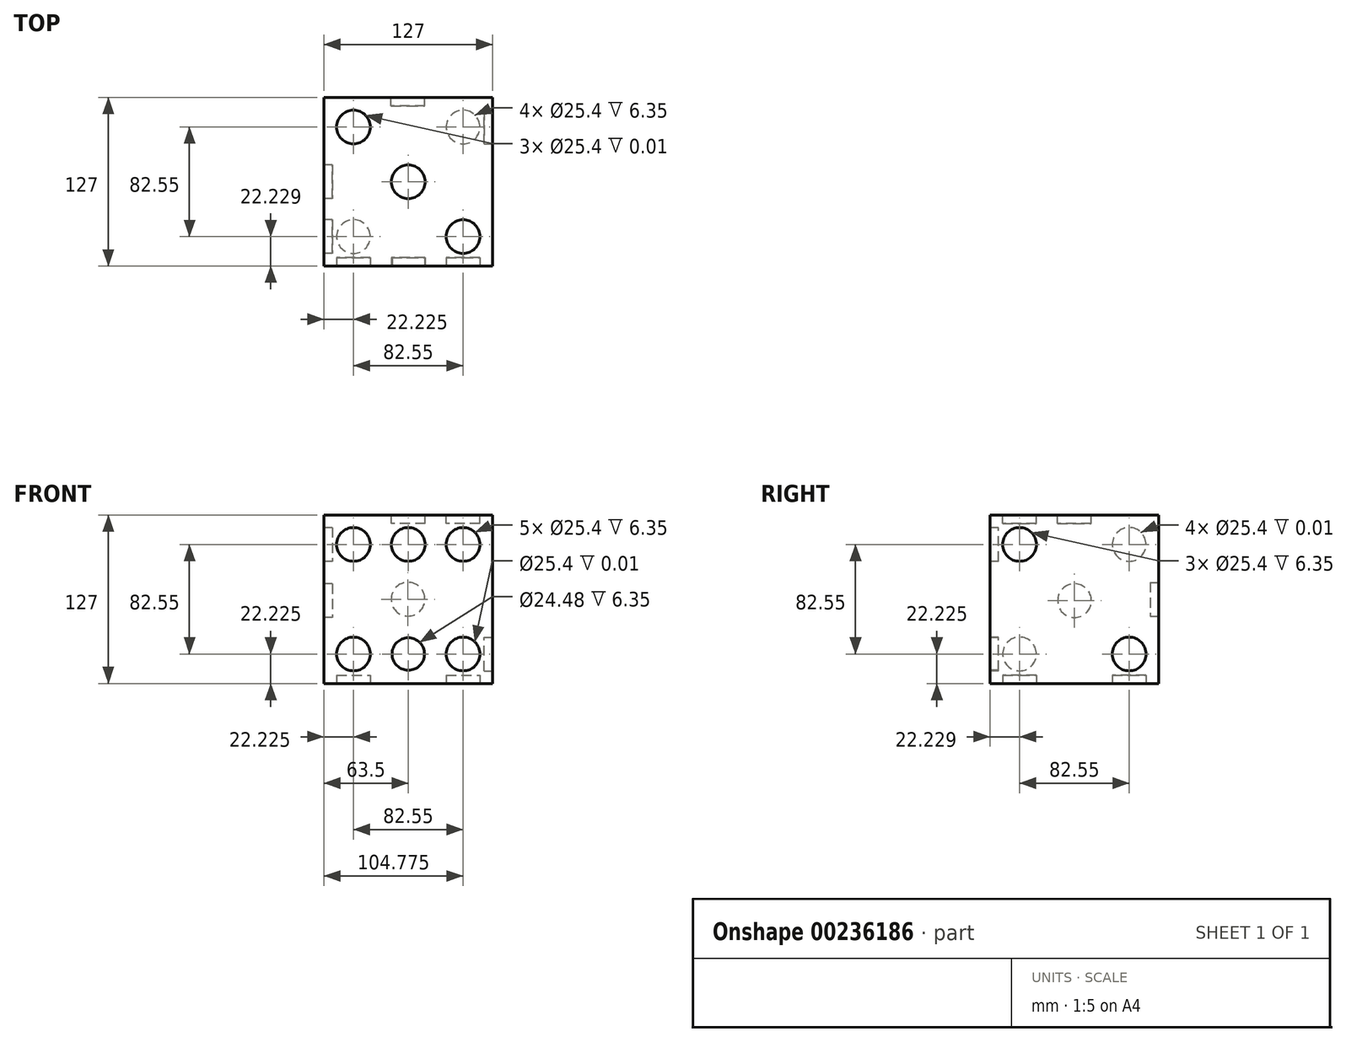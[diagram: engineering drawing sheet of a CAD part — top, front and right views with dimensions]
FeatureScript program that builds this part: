
annotation { "Feature Type Name" : "Feature", "Feature Type Description" : "" }
export const myFeature = defineFeature(function(context is Context, id is Id, definition is map)
    precondition{}
    {
        {
            var Q0;
            Q0=qCreatedBy(makeId("Right.planeOp"),FACE);
            var sketch = newSketch(context, id + "F0", { "sketchPlane" : qUnion([Q0])});
            skLineSegment(sketch, "E0.bottom", {"start": v(-65.66, 58.24) * mm, "end": v(61.34, 58.24) * mm});
            skLineSegment(sketch, "E0.top", {"start": v(-65.66, -68.76) * mm, "end": v(61.34, -68.76) * mm});
            skLineSegment(sketch, "E0.left", {"start": v(-65.66, 58.24) * mm, "end": v(-65.66, -68.76) * mm});
            skLineSegment(sketch, "E0.right", {"start": v(61.34, 58.24) * mm, "end": v(61.34, -68.76) * mm});
            skSolve(sketch);
        }
        {
            var Q0;
            Q0 = qSketchRegion(id + "F0", true);
            var Q1;
            Q1=makeQuery(id+"F0.imprint","IMPRINT",FACE,{"disambiguationData":[TD([[makeQuery(id+"F0.imprint","IMPRINT",EDGE,{"derivedFrom":sQuery(id+"F0.wireOp",EDGE,"E0.bottom")}),-1.0]])]});
            extrude(context, id + "F1", {"entities" : qUnion([Q0, Q1]), "depth" : 127 * mm});
        }
        {
            var Q0;
            Q0=makeQuery(id+"F1.opExtrude","SWEPT_FACE",FACE,{"disambiguationData":[OSD([sQuery(id+"F0.wireOp",EDGE,"E0.right")])]});
            var sketch = newSketch(context, id + "F2", { "sketchPlane" : qUnion([Q0])});
            skCircle(sketch, "E1", {"center": v(-63.28, -5.26) * mm, "radius": 12.7 * mm});
            skSolve(sketch);
        }
        {
            var Q0;
            Q0 = qSketchRegion(id + "F2", true);
            extrude(context, id + "F3", {"entities" : qUnion([Q0]), "operationType" : NewBodyOperationType.REMOVE, "oppositeDirection" : true, "depth" : 6.35 * mm});
        }
        {
            var Q0;
            Q0=makeQuery(id+"F1.opExtrude","CAP_FACE",FACE,{"disambiguationData":[OSD([sQuery(id+"F0.wireOp",EDGE,"E0.bottom"),sQuery(id+"F0.wireOp",EDGE,"E0.top"),sQuery(id+"F0.wireOp",EDGE,"E0.left"),sQuery(id+"F0.wireOp",EDGE,"E0.right")])],"isStart":true});
            var sketch = newSketch(context, id + "F4", { "sketchPlane" : qUnion([Q0])});
            skCircle(sketch, "E2", {"center": v(2.03, -6.35) * mm, "radius": 12.7 * mm});
            skSolve(sketch);
        }
        {
            var Q0;
            Q0 = qSketchRegion(id + "F4", true);
            extrude(context, id + "F5", {"entities" : qUnion([Q0]), "operationType" : NewBodyOperationType.REMOVE, "oppositeDirection" : true, "depth" : 6.35 * mm});
        }
        {
            var Q0;
            Q0=makeQuery(id+"F1.opExtrude","CAP_FACE",FACE,{"disambiguationData":[OSD([sQuery(id+"F0.wireOp",EDGE,"E0.bottom"),sQuery(id+"F0.wireOp",EDGE,"E0.top"),sQuery(id+"F0.wireOp",EDGE,"E0.left"),sQuery(id+"F0.wireOp",EDGE,"E0.right")])],"isStart":true});
            var sketch = newSketch(context, id + "F6", { "sketchPlane" : qUnion([Q0])});
            skCircle(sketch, "E3", {"center": v(-39.12, 36.01) * mm, "radius": 12.7 * mm});
            skSolve(sketch);
        }
        {
            var Q0;
            Q0 = qSketchRegion(id + "F6", true);
            extrude(context, id + "F7", {"entities" : qUnion([Q0]), "operationType" : NewBodyOperationType.REMOVE, "oppositeDirection" : true, "depth" : 1 / 101.6 * mm});
        }
        {
            var Q0;
            Q0=makeQuery(id+"F1.opExtrude","CAP_FACE",FACE,{"disambiguationData":[OSD([sQuery(id+"F0.wireOp",EDGE,"E0.bottom"),sQuery(id+"F0.wireOp",EDGE,"E0.top"),sQuery(id+"F0.wireOp",EDGE,"E0.left"),sQuery(id+"F0.wireOp",EDGE,"E0.right")])],"isStart":true});
            var sketch = newSketch(context, id + "F8", { "sketchPlane" : qUnion([Q0])});
            skCircle(sketch, "E4", {"center": v(43.43, 36.01) * mm, "radius": 12.7 * mm});
            skSolve(sketch);
        }
        {
            var Q0;
            Q0 = qSketchRegion(id + "F8", true);
            extrude(context, id + "F9", {"entities" : qUnion([Q0]), "operationType" : NewBodyOperationType.REMOVE, "oppositeDirection" : true, "depth" : 6.35 * mm});
        }
        {
            var Q0;
            Q0=makeQuery(id+"F1.opExtrude","CAP_FACE",FACE,{"disambiguationData":[OSD([sQuery(id+"F0.wireOp",EDGE,"E0.bottom"),sQuery(id+"F0.wireOp",EDGE,"E0.top"),sQuery(id+"F0.wireOp",EDGE,"E0.left"),sQuery(id+"F0.wireOp",EDGE,"E0.right")])],"isStart":true});
            var sketch = newSketch(context, id + "F10", { "sketchPlane" : qUnion([Q0])});
            skCircle(sketch, "E5", {"center": v(-39.12, -46.54) * mm, "radius": 12.7 * mm});
            skSolve(sketch);
        }
        {
            var Q0;
            Q0 = qSketchRegion(id + "F10", true);
            extrude(context, id + "F11", {"entities" : qUnion([Q0]), "operationType" : NewBodyOperationType.REMOVE, "oppositeDirection" : true, "depth" : 1 / 101.6 * mm});
        }
        {
            var Q0;
            Q0=makeQuery(id+"F1.opExtrude","CAP_FACE",FACE,{"disambiguationData":[OSD([sQuery(id+"F0.wireOp",EDGE,"E0.bottom"),sQuery(id+"F0.wireOp",EDGE,"E0.top"),sQuery(id+"F0.wireOp",EDGE,"E0.left"),sQuery(id+"F0.wireOp",EDGE,"E0.right")])],"isStart":true});
            var sketch = newSketch(context, id + "F12", { "sketchPlane" : qUnion([Q0])});
            skCircle(sketch, "E6", {"center": v(43.43, -46.54) * mm, "radius": 12.7 * mm});
            skSolve(sketch);
        }
        {
            var Q0;
            Q0 = qSketchRegion(id + "F12", true);
            extrude(context, id + "F13", {"entities" : qUnion([Q0]), "operationType" : NewBodyOperationType.REMOVE, "oppositeDirection" : true, "depth" : 1 / 101.6 * mm});
        }
        {
            var Q0;
            Q0=makeQuery(id+"F1.opExtrude","CAP_FACE",FACE,{"disambiguationData":[OSD([sQuery(id+"F0.wireOp",EDGE,"E0.bottom"),sQuery(id+"F0.wireOp",EDGE,"E0.top"),sQuery(id+"F0.wireOp",EDGE,"E0.left"),sQuery(id+"F0.wireOp",EDGE,"E0.right")])],"isStart":false});
            var sketch = newSketch(context, id + "F14", { "sketchPlane" : qUnion([Q0])});
            skCircle(sketch, "E7", {"center": v(39.12, -46.54) * mm, "radius": 12.7 * mm});
            skSolve(sketch);
        }
        {
            var Q0;
            Q0 = qSketchRegion(id + "F14", true);
            extrude(context, id + "F15", {"entities" : qUnion([Q0]), "operationType" : NewBodyOperationType.REMOVE, "oppositeDirection" : true, "depth" : 6.35 * mm});
        }
        {
            var Q0;
            Q0=makeQuery(id+"F1.opExtrude","CAP_FACE",FACE,{"disambiguationData":[OSD([sQuery(id+"F0.wireOp",EDGE,"E0.bottom"),sQuery(id+"F0.wireOp",EDGE,"E0.top"),sQuery(id+"F0.wireOp",EDGE,"E0.left"),sQuery(id+"F0.wireOp",EDGE,"E0.right")])],"isStart":false});
            var sketch = newSketch(context, id + "F16", { "sketchPlane" : qUnion([Q0])});
            skCircle(sketch, "E8", {"center": v(-43.43, 36.01) * mm, "radius": 12.7 * mm});
            skSolve(sketch);
        }
        {
            var Q0;
            Q0 = qSketchRegion(id + "F16", true);
            extrude(context, id + "F17", {"entities" : qUnion([Q0]), "operationType" : NewBodyOperationType.REMOVE, "oppositeDirection" : true, "depth" : 1 / 101.6 * mm});
        }
        {
            var Q0;
            Q0=makeQuery(id+"F1.opExtrude","SWEPT_FACE",FACE,{"disambiguationData":[OSD([sQuery(id+"F0.wireOp",EDGE,"E0.left")])]});
            var sketch = newSketch(context, id + "F18", { "sketchPlane" : qUnion([Q0])});
            skCircle(sketch, "E9", {"center": v(104.78, -46.54) * mm, "radius": 12.7 * mm});
            skSolve(sketch);
        }
        {
            var Q0;
            Q0 = qSketchRegion(id + "F18", true);
            extrude(context, id + "F19", {"entities" : qUnion([Q0]), "operationType" : NewBodyOperationType.REMOVE, "oppositeDirection" : true, "depth" : 1 / 101.6 * mm});
        }
        {
            var Q0;
            Q0=makeQuery(id+"F1.opExtrude","SWEPT_FACE",FACE,{"disambiguationData":[OSD([sQuery(id+"F0.wireOp",EDGE,"E0.left")])]});
            var sketch = newSketch(context, id + "F20", { "sketchPlane" : qUnion([Q0])});
            skCircle(sketch, "E10", {"center": v(63.5, -46.54) * mm, "radius": 12.24 * mm});
            skSolve(sketch);
        }
        {
            var Q0;
            Q0 = qSketchRegion(id + "F20", true);
            extrude(context, id + "F21", {"entities" : qUnion([Q0]), "operationType" : NewBodyOperationType.REMOVE, "oppositeDirection" : true, "depth" : 6.35 * mm});
        }
        {
            var Q0;
            Q0=makeQuery(id+"F1.opExtrude","SWEPT_FACE",FACE,{"disambiguationData":[OSD([sQuery(id+"F0.wireOp",EDGE,"E0.left")])]});
            var sketch = newSketch(context, id + "F22", { "sketchPlane" : qUnion([Q0])});
            skCircle(sketch, "E11", {"center": v(22.23, -46.54) * mm, "radius": 12.7 * mm});
            skSolve(sketch);
        }
        {
            var Q0;
            Q0 = qSketchRegion(id + "F22", true);
            extrude(context, id + "F23", {"entities" : qUnion([Q0]), "operationType" : NewBodyOperationType.REMOVE, "oppositeDirection" : true, "depth" : 6.35 * mm});
        }
        {
            var Q0;
            Q0=makeQuery(id+"F1.opExtrude","SWEPT_FACE",FACE,{"disambiguationData":[OSD([sQuery(id+"F0.wireOp",EDGE,"E0.left")])]});
            var sketch = newSketch(context, id + "F24", { "sketchPlane" : qUnion([Q0])});
            skSolve(sketch);
        }
        {
            var Q0;
            {var subQ0=sQuery(id+"F0.wireOp",EDGE,"E0.left");Q0=makeQuery(id+"F24.imprint","IMPRINT",FACE,{"disambiguationData":[TD([[makeQuery(id+"F24.imprint","IMPRINT",EDGE,{"derivedFrom":makeQuery(id+"F1.opExtrude","CAP_EDGE",EDGE,{"disambiguationData":[OSD([subQ0])],"isStart":true})}),1.0]])]});}
            var sketch = newSketch(context, id + "F25", { "sketchPlane" : qUnion([Q0])});
            skCircle(sketch, "E12", {"center": v(104.78, 36.01) * mm, "radius": 12.7 * mm});
            skSolve(sketch);
        }
        {
            var Q0;
            Q0 = qSketchRegion(id + "F25", true);
            extrude(context, id + "F26", {"entities" : qUnion([Q0]), "operationType" : NewBodyOperationType.REMOVE, "oppositeDirection" : true, "depth" : 6.35 * mm});
        }
        {
            var Q0;
            {var subQ0=sQuery(id+"F0.wireOp",EDGE,"E0.left");Q0=makeQuery(id+"F24.imprint","IMPRINT",FACE,{"disambiguationData":[TD([[makeQuery(id+"F24.imprint","IMPRINT",EDGE,{"derivedFrom":makeQuery(id+"F1.opExtrude","CAP_EDGE",EDGE,{"disambiguationData":[OSD([subQ0])],"isStart":true})}),1.0]])]});}
            var sketch = newSketch(context, id + "F27", { "sketchPlane" : qUnion([Q0])});
            skCircle(sketch, "E13", {"center": v(63.5, 36.01) * mm, "radius": 12.7 * mm});
            skSolve(sketch);
        }
        {
            var Q0;
            Q0 = qSketchRegion(id + "F27", true);
            extrude(context, id + "F28", {"entities" : qUnion([Q0]), "operationType" : NewBodyOperationType.REMOVE, "oppositeDirection" : true, "depth" : 6.35 * mm});
        }
        {
            var Q0;
            {var subQ0=sQuery(id+"F0.wireOp",EDGE,"E0.left");Q0=makeQuery(id+"F24.imprint","IMPRINT",FACE,{"disambiguationData":[TD([[makeQuery(id+"F24.imprint","IMPRINT",EDGE,{"derivedFrom":makeQuery(id+"F1.opExtrude","CAP_EDGE",EDGE,{"disambiguationData":[OSD([subQ0])],"isStart":true})}),1.0]])]});}
            var sketch = newSketch(context, id + "F29", { "sketchPlane" : qUnion([Q0])});
            skCircle(sketch, "E14", {"center": v(22.23, 36.01) * mm, "radius": 12.7 * mm});
            skSolve(sketch);
        }
        {
            var Q0;
            Q0 = qSketchRegion(id + "F29", true);
            extrude(context, id + "F30", {"entities" : qUnion([Q0]), "operationType" : NewBodyOperationType.REMOVE, "oppositeDirection" : true, "depth" : 6.35 * mm});
        }
        {
            var Q0;
            Q0=makeQuery(id+"F1.opExtrude","SWEPT_FACE",FACE,{"disambiguationData":[OSD([sQuery(id+"F0.wireOp",EDGE,"E0.bottom")])]});
            var sketch = newSketch(context, id + "F31", { "sketchPlane" : qUnion([Q0])});
            skCircle(sketch, "E15", {"center": v(104.78, -43.43) * mm, "radius": 12.7 * mm});
            skSolve(sketch);
        }
        {
            var Q0;
            Q0 = qSketchRegion(id + "F31", true);
            extrude(context, id + "F32", {"entities" : qUnion([Q0]), "operationType" : NewBodyOperationType.REMOVE, "oppositeDirection" : true, "depth" : 6.35 * mm});
        }
        {
            var Q0;
            Q0=makeQuery(id+"F1.opExtrude","SWEPT_FACE",FACE,{"disambiguationData":[OSD([sQuery(id+"F0.wireOp",EDGE,"E0.bottom")])]});
            var sketch = newSketch(context, id + "F33", { "sketchPlane" : qUnion([Q0])});
            skCircle(sketch, "E16", {"center": v(63.5, -2.16) * mm, "radius": 12.7 * mm});
            skSolve(sketch);
        }
        {
            var Q0;
            Q0 = qSketchRegion(id + "F33", true);
            extrude(context, id + "F34", {"entities" : qUnion([Q0]), "operationType" : NewBodyOperationType.REMOVE, "oppositeDirection" : true, "depth" : 6.35 * mm});
        }
        {
            var Q0;
            Q0=makeQuery(id+"F1.opExtrude","SWEPT_FACE",FACE,{"disambiguationData":[OSD([sQuery(id+"F0.wireOp",EDGE,"E0.bottom")])]});
            var sketch = newSketch(context, id + "F35", { "sketchPlane" : qUnion([Q0])});
            skCircle(sketch, "E17", {"center": v(22.23, 39.12) * mm, "radius": 12.7 * mm});
            skSolve(sketch);
        }
        {
            var Q0;
            Q0 = qSketchRegion(id + "F35", true);
            extrude(context, id + "F36", {"entities" : qUnion([Q0]), "operationType" : NewBodyOperationType.REMOVE, "oppositeDirection" : true, "depth" : 1 / 101.6 * mm});
        }
        {
            var Q0;
            Q0=makeQuery(id+"F1.opExtrude","SWEPT_FACE",FACE,{"disambiguationData":[OSD([sQuery(id+"F0.wireOp",EDGE,"E0.top")])]});
            var sketch = newSketch(context, id + "F37", { "sketchPlane" : qUnion([Q0])});
            skCircle(sketch, "E18", {"center": v(104.78, 43.43) * mm, "radius": 12.7 * mm});
            skSolve(sketch);
        }
        {
            var Q0;
            Q0 = qSketchRegion(id + "F37", true);
            extrude(context, id + "F38", {"entities" : qUnion([Q0]), "operationType" : NewBodyOperationType.REMOVE, "oppositeDirection" : true, "depth" : 1 / 101.6 * mm});
        }
        {
            var Q0;
            Q0=makeQuery(id+"F1.opExtrude","SWEPT_FACE",FACE,{"disambiguationData":[OSD([sQuery(id+"F0.wireOp",EDGE,"E0.top")])]});
            var sketch = newSketch(context, id + "F39", { "sketchPlane" : qUnion([Q0])});
            skCircle(sketch, "E19", {"center": v(22.23, 43.43) * mm, "radius": 12.7 * mm});
            skSolve(sketch);
        }
        {
            var Q0;
            Q0 = qSketchRegion(id + "F39", true);
            extrude(context, id + "F40", {"entities" : qUnion([Q0]), "operationType" : NewBodyOperationType.REMOVE, "oppositeDirection" : true, "depth" : 6.35 * mm});
        }
        {
            var Q0;
            Q0=makeQuery(id+"F1.opExtrude","SWEPT_FACE",FACE,{"disambiguationData":[OSD([sQuery(id+"F0.wireOp",EDGE,"E0.top")])]});
            var sketch = newSketch(context, id + "F41", { "sketchPlane" : qUnion([Q0])});
            skCircle(sketch, "E20", {"center": v(22.23, -39.12) * mm, "radius": 12.7 * mm});
            skSolve(sketch);
        }
        {
            var Q0;
            Q0 = qSketchRegion(id + "F41", true);
            extrude(context, id + "F42", {"entities" : qUnion([Q0]), "operationType" : NewBodyOperationType.REMOVE, "oppositeDirection" : true, "depth" : 1 / 101.6 * mm});
        }
        {
            var Q0;
            Q0=makeQuery(id+"F1.opExtrude","SWEPT_FACE",FACE,{"disambiguationData":[OSD([sQuery(id+"F0.wireOp",EDGE,"E0.top")])]});
            var sketch = newSketch(context, id + "F43", { "sketchPlane" : qUnion([Q0])});
            skCircle(sketch, "E21", {"center": v(104.78, -39.12) * mm, "radius": 12.7 * mm});
            skSolve(sketch);
        }
        {
            var Q0;
            Q0 = qSketchRegion(id + "F43", true);
            extrude(context, id + "F44", {"entities" : qUnion([Q0]), "operationType" : NewBodyOperationType.REMOVE, "oppositeDirection" : true, "depth" : 6.35 * mm});
        }
    });
